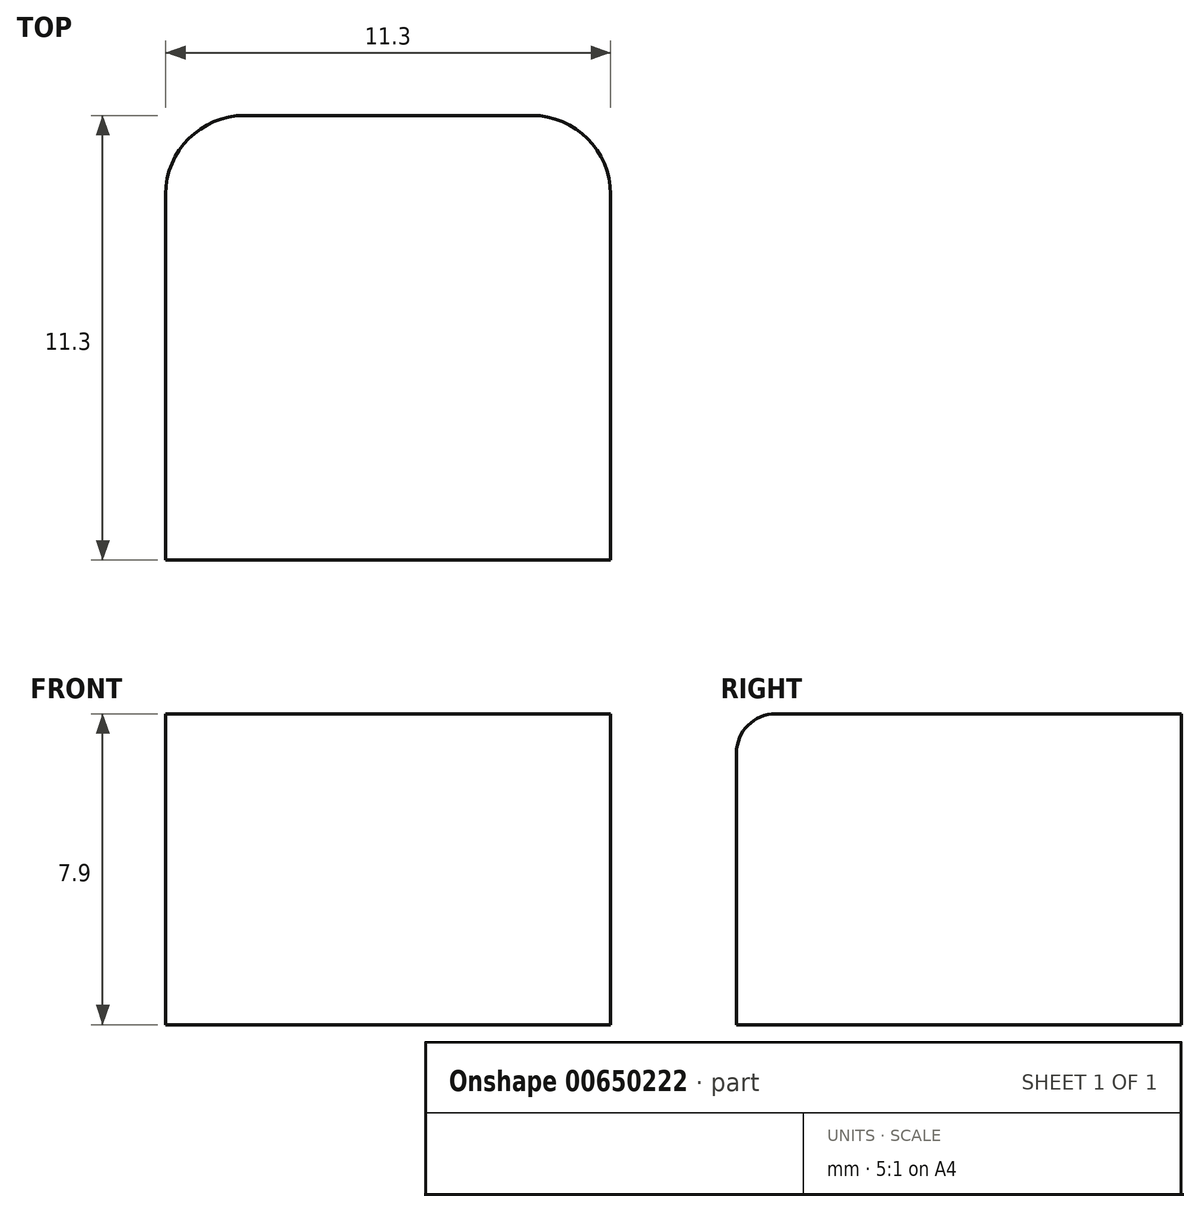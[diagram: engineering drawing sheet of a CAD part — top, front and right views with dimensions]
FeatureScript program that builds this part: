
annotation { "Feature Type Name" : "Feature", "Feature Type Description" : "" }
export const myFeature = defineFeature(function(context is Context, id is Id, definition is map)
    precondition{}
    {
        {
            var Q0;
            Q0=qCreatedBy(makeId("Top.planeOp"),FACE);
            var sketch = newSketch(context, id + "F0", { "sketchPlane" : qUnion([Q0])});
            skLineSegment(sketch, "E0.bottom", {"start": v(0, 0) * mm, "end": v(11.3, 0) * mm});
            skLineSegment(sketch, "E0.top", {"start": v(0, 19.2) * mm, "end": v(11.3, 19.2) * mm});
            skLineSegment(sketch, "E0.left", {"start": v(0, 0) * mm, "end": v(0, 19.2) * mm});
            skLineSegment(sketch, "E0.right", {"start": v(11.3, 0) * mm, "end": v(11.3, 19.2) * mm});
            skSolve(sketch);
        }
        {
            var Q0;
            Q0=makeQuery(id+"F0.imprint","IMPRINT",FACE,{"disambiguationData":[TD([[makeQuery(id+"F0.imprint","IMPRINT",EDGE,{"derivedFrom":sQuery(id+"F0.wireOp",EDGE,"E0.bottom")}),1.0]])]});
            extrude(context, id + "F1", {"entities" : qUnion([Q0]), "depth" : 11.3 * mm, "offsetDistance" : 25 * mm});
        }
        {
            var Q0;
            Q0=makeQuery(id+"F1.opExtrude","CAP_FACE",FACE,{"disambiguationData":[OSD([sQuery(id+"F0.wireOp",EDGE,"E0.bottom"),sQuery(id+"F0.wireOp",EDGE,"E0.top"),sQuery(id+"F0.wireOp",EDGE,"E0.left"),sQuery(id+"F0.wireOp",EDGE,"E0.right")])],"isStart":false});
            var sketch = newSketch(context, id + "F2", { "sketchPlane" : qUnion([Q0])});
            skLineSegment(sketch, "E1.bottom", {"start": v(0, 0) * mm, "end": v(11.3, 0) * mm});
            skLineSegment(sketch, "E1.top", {"start": v(0, 11.3) * mm, "end": v(11.3, 11.3) * mm});
            skLineSegment(sketch, "E1.left", {"start": v(0, 0) * mm, "end": v(0, 11.3) * mm});
            skLineSegment(sketch, "E1.right", {"start": v(11.3, 0) * mm, "end": v(11.3, 11.3) * mm});
            skSolve(sketch);
        }
        {
            var Q0;
            Q0=makeQuery(id+"F2.imprint","IMPRINT",FACE,{"disambiguationData":[TD([[makeQuery(id+"F2.imprint","IMPRINT",EDGE,{"derivedFrom":sQuery(id+"F2.wireOp",EDGE,"E1.bottom")}),1.0]])]});
            extrude(context, id + "F3", {"entities" : qUnion([Q0]), "operationType" : NewBodyOperationType.REMOVE, "oppositeDirection" : true, "depth" : 25 * mm, "offsetDistance" : 25 * mm});
        }
        {
            var Q0;
            Q0=makeQuery(id+"F1.opExtrude","CAP_EDGE",EDGE,{"disambiguationData":[OSD([sQuery(id+"F0.wireOp",EDGE,"E0.right")])],"isStart":true});
            var Q1;
            Q1=makeQuery(id+"F1.opExtrude","CAP_EDGE",EDGE,{"disambiguationData":[OSD([sQuery(id+"F0.wireOp",EDGE,"E0.left")])],"isStart":true});
            fillet(context, id + "F4", {"entities" : qUnion([Q0, Q1]), "radius" : 2 * mm, "tangentPropagation" : true, "allowEdgeOverflow" : false});
        }
        {
            var Q0;
            Q0=makeQuery(id+"F1.opExtrude","CAP_EDGE",EDGE,{"disambiguationData":[OSD([sQuery(id+"F0.wireOp",EDGE,"E0.top")])],"isStart":false});
            fillet(context, id + "F5", {"entities" : qUnion([Q0]), "radius" : 1 * mm, "tangentPropagation" : true, "allowEdgeOverflow" : false});
        }
        {
            var Q0;
            Q0=makeQuery(id+"F1.opExtrude","SWEPT_BODY",BODY,{"disambiguationData":[OSD([sQuery(id+"F0.wireOp",EDGE,"E0.bottom"),sQuery(id+"F0.wireOp",EDGE,"E0.top"),sQuery(id+"F0.wireOp",EDGE,"E0.left"),sQuery(id+"F0.wireOp",EDGE,"E0.right")])]});
            var Q1;
            Q1=makeQuery(id+"F3.boolean.opBoolean","INTERSECT",EDGE,{"derivedFrom":[makeQuery(id+"F1.opExtrude","CAP_FACE",FACE,{"disambiguationData":[OSD([sQuery(id+"F0.wireOp",EDGE,"E0.bottom"),sQuery(id+"F0.wireOp",EDGE,"E0.top"),sQuery(id+"F0.wireOp",EDGE,"E0.left"),sQuery(id+"F0.wireOp",EDGE,"E0.right")])],"isStart":true}),makeQuery(id+"F3.opExtrude","SWEPT_FACE",FACE,{"disambiguationData":[OSD([sQuery(id+"F2.wireOp",EDGE,"E1.top")])]})]});
            transform(context, id + "F6", {"entities" : qUnion([Q0]), "transformType" : TransformType.ROTATION, "transformAxis" : qUnion([Q1]), "angle" : 90 * degree, "makeCopy" : false});
        }
    });
